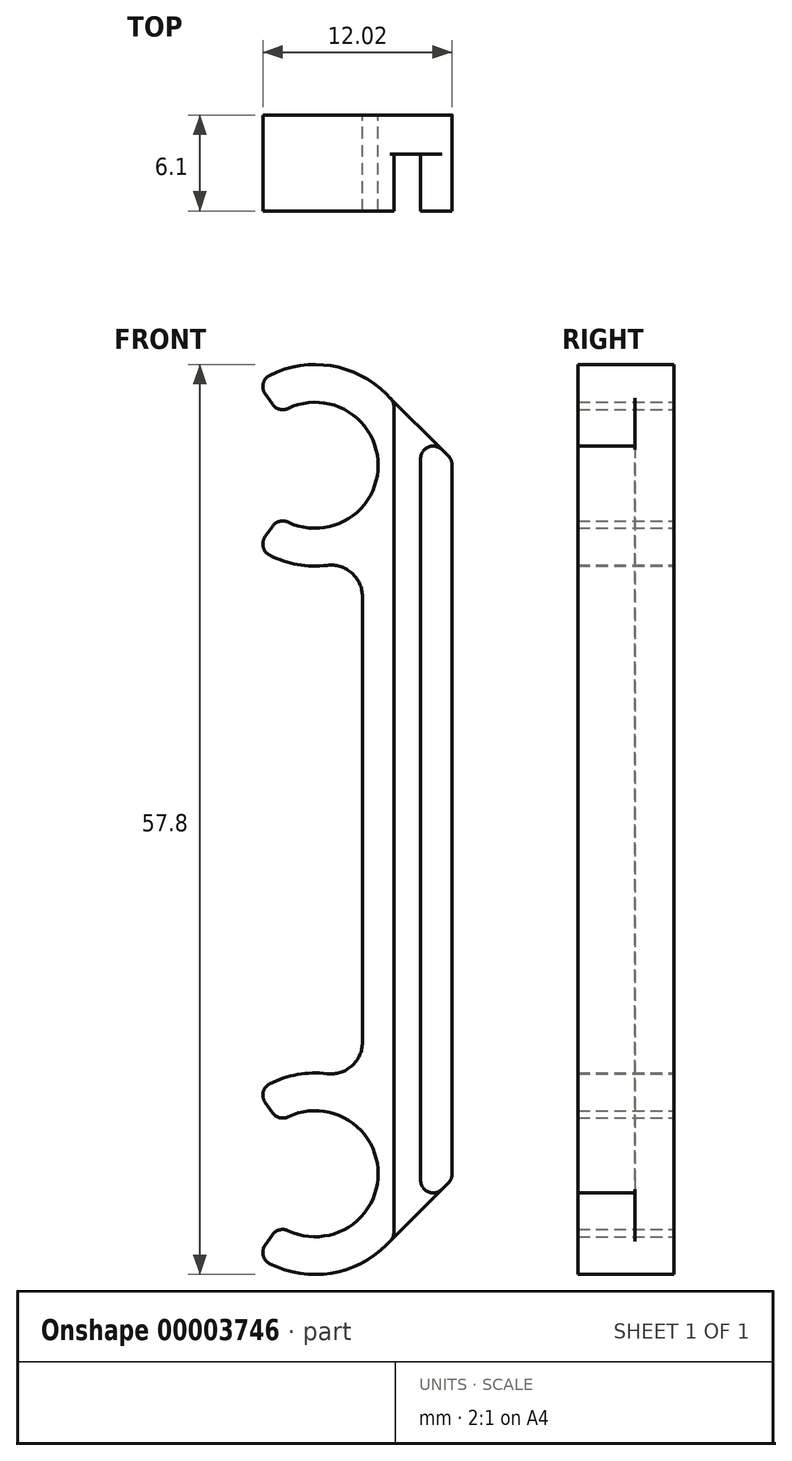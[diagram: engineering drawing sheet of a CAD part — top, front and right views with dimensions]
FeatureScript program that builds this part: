
annotation { "Feature Type Name" : "Feature", "Feature Type Description" : "" }
export const myFeature = defineFeature(function(context is Context, id is Id, definition is map)
    precondition{}
    {
        {
            var Q0;
            Q0=qCreatedBy(makeId("Front.planeOp"),FACE);
            var sketch = newSketch(context, id + "F0", { "sketchPlane" : qUnion([Q0])});
            skArc(sketch, "E0", {"start": v(-2.3, 41.72) * mm, "mid": v(4, 45) * mm, "end": v(-2.3, 48.28) * mm});
            skArc(sketch, "E1", {"start": v(-2.3, -3.28) * mm, "mid": v(4, 0) * mm, "end": v(-2.3, 3.28) * mm});
            skArc(sketch, "E2", {"start": v(0.76, 6.35) * mm, "mid": v(-1.56, 6.2) * mm, "end": v(-3.67, 5.24) * mm});
            skArc(sketch, "E3", {"start": v(4.53, 49.53) * mm, "mid": v(0.56, 51.38) * mm, "end": v(-3.67, 50.24) * mm});
            skLineSegment(sketch, "E4", {"start": v(5, -4.05) * mm, "end": v(5, 49.05) * mm});
            skPoint(sketch, "E5.orphan", {"position": v(4, 0) * mm});
            skLineSegment(sketch, "E6", {"start": v(-2.3, 3.28) * mm, "end": v(-3.67, 5.24) * mm});
            skLineSegment(sketch, "E7", {"start": v(0, 0) * mm, "end": v(-6.4, 0) * mm, "construction": true});
            skLineSegment(sketch, "E8.0.MirrorCS", {"start": v(-2.3, -3.28) * mm, "end": v(-3.67, -5.24) * mm});
            skLineSegment(sketch, "E9", {"start": v(8.7, 22.5) * mm, "end": v(-6.4, 22.5) * mm, "construction": true});
            skArc(sketch, "E10.trimOffspring", {"start": v(-3.67, -5.24) * mm, "mid": v(0.56, -6.38) * mm, "end": v(4.53, -4.53) * mm});
            skLineSegment(sketch, "E11.0.MirrorCS", {"start": v(-2.3, 48.28) * mm, "end": v(-3.67, 50.24) * mm});
            skLineSegment(sketch, "E12.0.MirrorCS", {"start": v(-2.3, 41.72) * mm, "end": v(-3.67, 39.76) * mm});
            skArc(sketch, "E13.trimOffspring", {"start": v(-3.67, 39.76) * mm, "mid": v(-1.56, 38.8) * mm, "end": v(0.76, 38.65) * mm});
            skLineSegment(sketch, "E14", {"start": v(4.53, 49.53) * mm, "end": v(8.7, 45.35) * mm});
            skLineSegment(sketch, "E15.0.MirrorCS", {"start": v(4.53, -4.53) * mm, "end": v(8.7, -0.35) * mm});
            skLineSegment(sketch, "E16.trimOffspring", {"start": v(6.7, 47.35) * mm, "end": v(6.7, -2.35) * mm});
            skPoint(sketch, "E17.visualSharp", {"position": v(8.7, -0.35) * mm});
            skLineSegment(sketch, "E18.0", {"start": v(8.7, 45.35) * mm, "end": v(8.7, -0.35) * mm});
            skLineSegment(sketch, "E19", {"start": v(3, 36.66) * mm, "end": v(3, 8.34) * mm});
            skArc(sketch, "E20.filletArc", {"start": v(0.76, 6.35) * mm, "mid": v(2.33, 6.84) * mm, "end": v(3, 8.34) * mm});
            skArc(sketch, "E21.filletArc", {"start": v(3, 36.66) * mm, "mid": v(2.33, 38.16) * mm, "end": v(0.76, 38.65) * mm});
            skSolve(sketch);
        }
        {
            var Q0;
            Q0=makeQuery(id+"F0.imprint","IMPRINT",FACE,{"disambiguationData":[TD([[makeQuery(id+"F0.imprint","IMPRINT",EDGE,{"derivedFrom":sQuery(id+"F0.wireOp",EDGE,"E0")}),-1.0]])]});
            var Q1;
            Q1=makeQuery(id+"F0.imprint","IMPRINT",FACE,{"disambiguationData":[TD([[makeQuery(id+"F0.imprint","IMPRINT",EDGE,{"derivedFrom":sQuery(id+"F0.wireOp",EDGE,"dfa2cc31-a6e8-46c3-b2ce-c2e06a46fc66")}),-1.0]])]});
            var Q2;
            {var subQ1=sQuery(id+"F0.wireOp",EDGE,"1ba8ad5c-b601-476a-9779-88b53e210d94");Q2=makeQuery(id+"F0.imprint","IMPRINT",FACE,{"disambiguationData":[TD([[makeQuery(id+"F0.imprint","IMPRINT",EDGE,{"derivedFrom":subQ1}),1.0]])]});}
            var Q3;
            Q3=makeQuery(id+"F0.imprint","IMPRINT",FACE,{"disambiguationData":[TD([[makeQuery(id+"F0.imprint","IMPRINT",EDGE,{"derivedFrom":sQuery(id+"F0.wireOp",EDGE,"dfa2cc31-a6e8-46c3-b2ce-c2e06a46fc66")}),1.0]])]});
            var Q4;
            {var subQ4=sQuery(id+"F0.wireOp",EDGE,"aa7d58d1-2776-434c-a1b8-937a125aae7e.0.MirrorCS");Q4=makeQuery(id+"F0.imprint","IMPRINT",FACE,{"disambiguationData":[TD([[makeQuery(id+"F0.imprint","IMPRINT",EDGE,{"derivedFrom":subQ4}),-1.0]])]});}
            var Q5;
            {var subQ3=sQuery(id+"F0.wireOp",EDGE,"695c2fa7-dfbd-4be1-8a4d-e9ee8b981d7d");Q5=makeQuery(id+"F0.imprint","IMPRINT",FACE,{"disambiguationData":[TD([[makeQuery(id+"F0.imprint","IMPRINT",EDGE,{"derivedFrom":subQ3}),1.0]])]});}
            var Q6;
            Q6=makeQuery(id+"F0.imprint","IMPRINT",FACE,{"disambiguationData":[TD([[makeQuery(id+"F0.imprint","IMPRINT",EDGE,{"derivedFrom":sQuery(id+"F0.wireOp",EDGE,"2eeb60b7-0f88-4b5b-8cb8-60df6ddea03d")}),-1.0]])]});
            var Q7;
            {var subQ2=sQuery(id+"F0.wireOp",EDGE,"E4");Q7=makeQuery(id+"F0.imprint","IMPRINT",FACE,{"disambiguationData":[TD([[makeQuery(id+"F0.imprint","IMPRINT",EDGE,{"derivedFrom":subQ2}),-1.0]])]});}
            var Q8;
            {var subQ1=sQuery(id+"F0.wireOp",EDGE,"E16.trimOffspring");Q8=makeQuery(id+"F0.imprint","IMPRINT",FACE,{"disambiguationData":[TD([[makeQuery(id+"F0.imprint","IMPRINT",EDGE,{"derivedFrom":subQ1}),1.0]])]});}
            extrude(context, id + "F1", {"entities" : qUnion([Q0, Q1, Q2, Q3, Q4, Q5, Q6, Q7, Q8]), "depth" : 2.5 * mm});
        }
        {
            var Q0;
            Q0=makeQuery(id+"F0.imprint","IMPRINT",FACE,{"disambiguationData":[TD([[makeQuery(id+"F0.imprint","IMPRINT",EDGE,{"derivedFrom":sQuery(id+"F0.wireOp",EDGE,"dfa2cc31-a6e8-46c3-b2ce-c2e06a46fc66")}),1.0]])]});
            var Q1;
            Q1=makeQuery(id+"F0.imprint","IMPRINT",FACE,{"disambiguationData":[TD([[makeQuery(id+"F0.imprint","IMPRINT",EDGE,{"derivedFrom":sQuery(id+"F0.wireOp",EDGE,"E0")}),-1.0]])]});
            var Q2;
            {var subQ4=sQuery(id+"F0.wireOp",EDGE,"aa7d58d1-2776-434c-a1b8-937a125aae7e.0.MirrorCS");Q2=makeQuery(id+"F0.imprint","IMPRINT",FACE,{"disambiguationData":[TD([[makeQuery(id+"F0.imprint","IMPRINT",EDGE,{"derivedFrom":subQ4}),-1.0]])]});}
            var Q3;
            Q3=makeQuery(id+"F0.imprint","IMPRINT",FACE,{"disambiguationData":[TD([[makeQuery(id+"F0.imprint","IMPRINT",EDGE,{"derivedFrom":sQuery(id+"F0.wireOp",EDGE,"2eeb60b7-0f88-4b5b-8cb8-60df6ddea03d")}),-1.0]])]});
            var Q4;
            {var subQ1=sQuery(id+"F0.wireOp",EDGE,"E16.trimOffspring");Q4=makeQuery(id+"F0.imprint","IMPRINT",FACE,{"disambiguationData":[TD([[makeQuery(id+"F0.imprint","IMPRINT",EDGE,{"derivedFrom":subQ1}),1.0]])]});}
            extrude(context, id + "F2", {"entities" : qUnion([Q0, Q1, Q2, Q3, Q4]), "operationType" : NewBodyOperationType.ADD, "depth" : (3.6 + 2.5) * mm});
        }
        {
            var Q0;
            {var subQ0=sQuery(id+"F0.wireOp",EDGE,"E3");var subQ1=sQuery(id+"F0.wireOp",EDGE,"E14");var subQ2=sQuery(id+"F0.wireOp",EDGE,"E18.0");Q0=qUnion([makeQuery(id+"F2.boolean.opBoolean","MERGE",EDGE,{"derivedFrom":[makeQuery(id+"F1.opExtrude","SWEPT_EDGE",EDGE,{"disambiguationData":[OSD([subQ0,subQ1])]}),makeQuery(id+"F2.opExtrude","SWEPT_EDGE",EDGE,{"disambiguationData":[OSD([subQ0,subQ1])]})]}),makeQuery(id+"F2.boolean.opBoolean","MERGE",EDGE,{"derivedFrom":[makeQuery(id+"F1.opExtrude","SWEPT_EDGE",EDGE,{"disambiguationData":[OSD([subQ1,subQ2])]}),makeQuery(id+"F2.opExtrude","SWEPT_EDGE",EDGE,{"disambiguationData":[OSD([subQ1,subQ2])]})]}),makeQuery(id+"F2.opExtrude","SWEPT_EDGE",EDGE,{"disambiguationData":[OSD([sQuery(id+"F0.wireOp",EDGE,"E4"),subQ1])]}),makeQuery(id+"F2.opExtrude","SWEPT_EDGE",EDGE,{"disambiguationData":[OSD([subQ1,sQuery(id+"F0.wireOp",EDGE,"E16.trimOffspring")])]})]);}
            var Q1;
            Q1=makeQuery(id+"F2.opExtrude","SWEPT_EDGE",EDGE,{"disambiguationData":[OSD([sQuery(id+"F0.wireOp",EDGE,"E15.0.MirrorCS"),sQuery(id+"F0.wireOp",EDGE,"E16.trimOffspring")])]});
            var Q2;
            {var subQ0=sQuery(id+"F0.wireOp",EDGE,"E3");var subQ1=sQuery(id+"F0.wireOp",EDGE,"E11.0.MirrorCS");Q2=makeQuery(id+"F2.boolean.opBoolean","MERGE",EDGE,{"derivedFrom":[makeQuery(id+"F1.opExtrude","SWEPT_EDGE",EDGE,{"disambiguationData":[OSD([subQ0,subQ1])]}),makeQuery(id+"F2.opExtrude","SWEPT_EDGE",EDGE,{"disambiguationData":[OSD([subQ0,subQ1])]})]});}
            var Q3;
            {var subQ0=sQuery(id+"F0.wireOp",EDGE,"E0");var subQ1=sQuery(id+"F0.wireOp",EDGE,"E11.0.MirrorCS");Q3=makeQuery(id+"F2.boolean.opBoolean","MERGE",EDGE,{"derivedFrom":[makeQuery(id+"F1.opExtrude","SWEPT_EDGE",EDGE,{"disambiguationData":[OSD([subQ0,subQ1])]}),makeQuery(id+"F2.opExtrude","SWEPT_EDGE",EDGE,{"disambiguationData":[OSD([subQ0,subQ1])]})]});}
            var Q4;
            {var subQ0=sQuery(id+"F0.wireOp",EDGE,"E0");var subQ1=sQuery(id+"F0.wireOp",EDGE,"E12.0.MirrorCS");Q4=makeQuery(id+"F2.boolean.opBoolean","MERGE",EDGE,{"derivedFrom":[makeQuery(id+"F1.opExtrude","SWEPT_EDGE",EDGE,{"disambiguationData":[OSD([subQ0,subQ1])]}),makeQuery(id+"F2.opExtrude","SWEPT_EDGE",EDGE,{"disambiguationData":[OSD([subQ0,subQ1])]})]});}
            var Q5;
            {var subQ0=sQuery(id+"F0.wireOp",EDGE,"E12.0.MirrorCS");var subQ1=sQuery(id+"F0.wireOp",EDGE,"E13.trimOffspring");Q5=makeQuery(id+"F2.boolean.opBoolean","MERGE",EDGE,{"derivedFrom":[makeQuery(id+"F1.opExtrude","SWEPT_EDGE",EDGE,{"disambiguationData":[OSD([subQ0,subQ1])]}),makeQuery(id+"F2.opExtrude","SWEPT_EDGE",EDGE,{"disambiguationData":[OSD([subQ0,subQ1])]})]});}
            var Q6;
            {var subQ0=sQuery(id+"F0.wireOp",EDGE,"E2");var subQ1=sQuery(id+"F0.wireOp",EDGE,"E6");Q6=makeQuery(id+"F2.boolean.opBoolean","MERGE",EDGE,{"derivedFrom":[makeQuery(id+"F1.opExtrude","SWEPT_EDGE",EDGE,{"disambiguationData":[OSD([subQ0,subQ1])]}),makeQuery(id+"F2.opExtrude","SWEPT_EDGE",EDGE,{"disambiguationData":[OSD([subQ0,subQ1])]})]});}
            var Q7;
            {var subQ0=sQuery(id+"F0.wireOp",EDGE,"E1");var subQ1=sQuery(id+"F0.wireOp",EDGE,"E6");Q7=makeQuery(id+"F2.boolean.opBoolean","MERGE",EDGE,{"derivedFrom":[makeQuery(id+"F1.opExtrude","SWEPT_EDGE",EDGE,{"disambiguationData":[OSD([subQ0,subQ1])]}),makeQuery(id+"F2.opExtrude","SWEPT_EDGE",EDGE,{"disambiguationData":[OSD([subQ0,subQ1])]})]});}
            var Q8;
            {var subQ0=sQuery(id+"F0.wireOp",EDGE,"E1");var subQ1=sQuery(id+"F0.wireOp",EDGE,"E8.0.MirrorCS");Q8=makeQuery(id+"F2.boolean.opBoolean","MERGE",EDGE,{"derivedFrom":[makeQuery(id+"F1.opExtrude","SWEPT_EDGE",EDGE,{"disambiguationData":[OSD([subQ0,subQ1])]}),makeQuery(id+"F2.opExtrude","SWEPT_EDGE",EDGE,{"disambiguationData":[OSD([subQ0,subQ1])]})]});}
            var Q9;
            {var subQ0=sQuery(id+"F0.wireOp",EDGE,"E8.0.MirrorCS");var subQ1=sQuery(id+"F0.wireOp",EDGE,"E10.trimOffspring");Q9=makeQuery(id+"F2.boolean.opBoolean","MERGE",EDGE,{"derivedFrom":[makeQuery(id+"F1.opExtrude","SWEPT_EDGE",EDGE,{"disambiguationData":[OSD([subQ0,subQ1])]}),makeQuery(id+"F2.opExtrude","SWEPT_EDGE",EDGE,{"disambiguationData":[OSD([subQ0,subQ1])]})]});}
            var Q10;
            Q10=makeQuery(id+"F2.opExtrude","SWEPT_EDGE",EDGE,{"disambiguationData":[OSD([sQuery(id+"F0.wireOp",EDGE,"E4"),sQuery(id+"F0.wireOp",EDGE,"E15.0.MirrorCS")])]});
            var Q11;
            {var subQ0=sQuery(id+"F0.wireOp",EDGE,"E15.0.MirrorCS");var subQ1=sQuery(id+"F0.wireOp",EDGE,"E18.0");Q11=makeQuery(id+"F2.boolean.opBoolean","MERGE",EDGE,{"derivedFrom":[makeQuery(id+"F1.opExtrude","SWEPT_EDGE",EDGE,{"disambiguationData":[OSD([subQ0,subQ1])]}),makeQuery(id+"F2.opExtrude","SWEPT_EDGE",EDGE,{"disambiguationData":[OSD([subQ0,subQ1])]})]});}
            fillet(context, id + "F3", {"entities" : qUnion([Q0, Q1, Q2, Q3, Q4, Q5, Q6, Q7, Q8, Q9, Q10, Q11]), "radius" : 0.8 * mm, "tangentPropagation" : true, "allowEdgeOverflow" : false});
        }
    });
